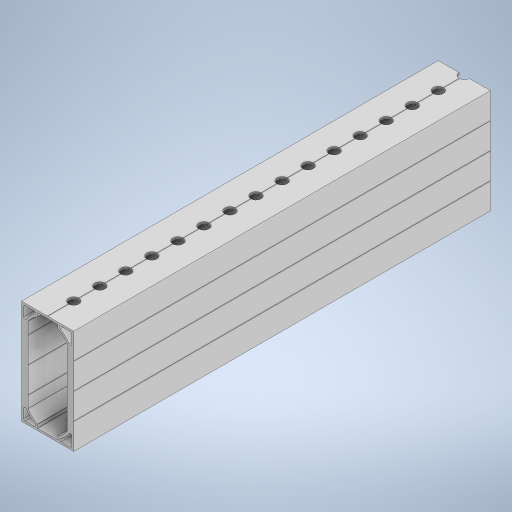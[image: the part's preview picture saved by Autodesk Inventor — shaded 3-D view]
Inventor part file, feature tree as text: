
AUTODESK INVENTOR PART (.ipt)
format: ipt  version: 2023.4 (Build 274418000, 418)  size: 762,880 bytes
history: native  units: in
note: dims shown in document units (in); Inventor stores cm internally (conversion verified against a paired STEP export)
features: extrude x1, sketch x1, other x1
ambient origin geometry x8: Origin, YZ Plane, XZ Plane, XY Plane, X Axis, Y Axis, Z Axis, Center Point
bodies: Solid1 (feature_tree)
feature tree (3):
  extrude  "Extrusion1"  [1 undecoded]
  sketch  "Sketch1"  dims[d0=39.0in d1=0.0in]
  other  "Internal Fillets"
note: 1 required parameter value undecoded (feature->parameter linkage not recoverable at this tier; creation-order binding heuristic only, values carry confidence <= 0.55)
